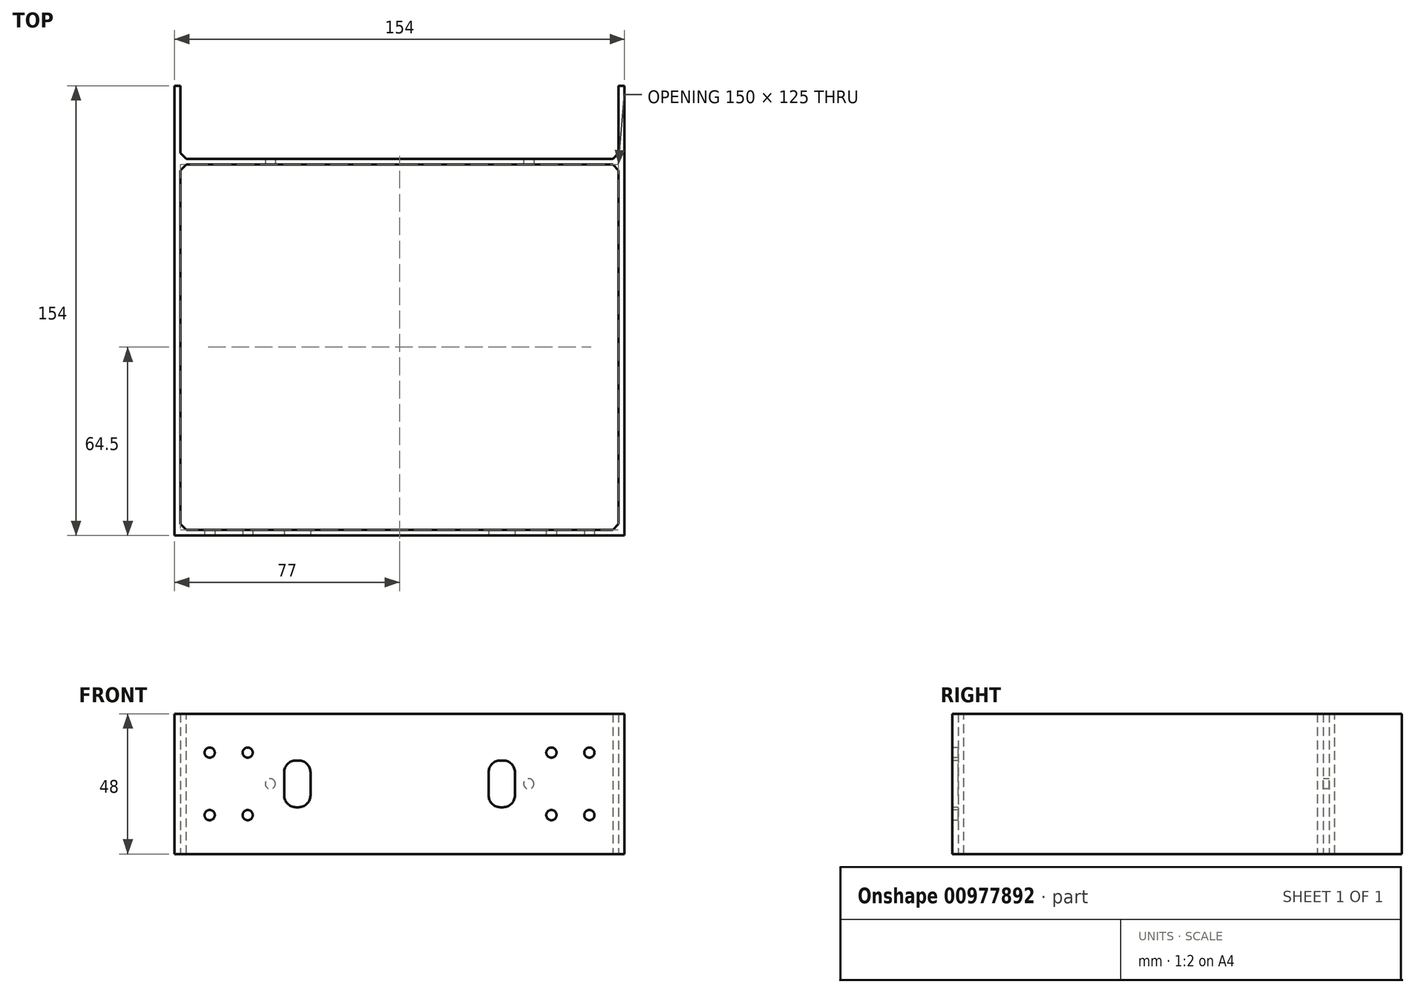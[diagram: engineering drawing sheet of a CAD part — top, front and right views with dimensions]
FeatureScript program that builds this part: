
annotation { "Feature Type Name" : "Feature", "Feature Type Description" : "" }
export const myFeature = defineFeature(function(context is Context, id is Id, definition is map)
    precondition{}
    {
        {
            var Q0;
            Q0=qCreatedBy(makeId("Top.planeOp"),FACE);
            var sketch = newSketch(context, id + "F0", { "sketchPlane" : qUnion([Q0])});
            skLineSegment(sketch, "E0.bottom", {"start": v(75, -62.5) * mm, "end": v(-75, -62.5) * mm});
            skLineSegment(sketch, "E0.top", {"start": v(75, 62.5) * mm, "end": v(-75, 62.5) * mm});
            skLineSegment(sketch, "E0.left", {"start": v(75, -62.5) * mm, "end": v(75, 62.5) * mm});
            skLineSegment(sketch, "E0.right", {"start": v(-75, -62.5) * mm, "end": v(-75, 62.5) * mm});
            skPoint(sketch, "E0.middle", {"position": v(0, 0) * mm});
            skLineSegment(sketch, "E1.0", {"start": v(75, 64.5) * mm, "end": v(-75, 64.5) * mm});
            skLineSegment(sketch, "E1.1", {"start": v(77, -64.5) * mm, "end": v(77, 64.5) * mm});
            skLineSegment(sketch, "E1.2", {"start": v(77, -64.5) * mm, "end": v(-77, -64.5) * mm});
            skLineSegment(sketch, "E1.3", {"start": v(-77, -64.5) * mm, "end": v(-77, 64.5) * mm});
            skLineSegment(sketch, "E2", {"start": v(-77, 64.5) * mm, "end": v(-77, 89.5) * mm});
            skLineSegment(sketch, "E3", {"start": v(-77, 89.5) * mm, "end": v(-75, 89.5) * mm});
            skLineSegment(sketch, "E4", {"start": v(-75, 89.5) * mm, "end": v(-75, 64.5) * mm});
            skLineSegment(sketch, "E5", {"start": v(77, 64.5) * mm, "end": v(77, 89.5) * mm});
            skLineSegment(sketch, "E6", {"start": v(77, 89.5) * mm, "end": v(75, 89.5) * mm});
            skLineSegment(sketch, "E7", {"start": v(75, 89.5) * mm, "end": v(75, 64.5) * mm});
            skSolve(sketch);
        }
        {
            var Q0;
            Q0=makeQuery(id+"F0.imprint","IMPRINT",FACE,{"disambiguationData":[TD([[makeQuery(id+"F0.imprint","IMPRINT",EDGE,{"derivedFrom":sQuery(id+"F0.wireOp",EDGE,"E0.bottom")}),1.0]])]});
            extrude(context, id + "F1", {"entities" : qUnion([Q0]), "depth" : 48 * mm, "offsetDistance" : 25 * mm});
        }
        {
            var Q0;
            Q0=makeQuery(id+"F1.opExtrude","SWEPT_FACE",FACE,{"disambiguationData":[OSD([sQuery(id+"F0.wireOp",EDGE,"E1.2")])]});
            var sketch = newSketch(context, id + "F2", { "sketchPlane" : qUnion([Q0])});
            skPoint(sketch, "E8", {"position": v(-65, 34.7) * mm});
            skPoint(sketch, "E9", {"position": v(-52, 34.7) * mm});
            skPoint(sketch, "E10", {"position": v(-65, 13.3) * mm});
            skPoint(sketch, "E11", {"position": v(-52, 13.3) * mm});
            skCircle(sketch, "E12", {"center": v(-65, 34.7) * mm, "radius": 1.75 * mm});
            skCircle(sketch, "E13", {"center": v(-52, 34.7) * mm, "radius": 1.75 * mm});
            skCircle(sketch, "E14", {"center": v(-65, 13.3) * mm, "radius": 1.75 * mm});
            skCircle(sketch, "E15", {"center": v(-52, 13.3) * mm, "radius": 1.75 * mm});
            skPoint(sketch, "E16", {"position": v(65, 34.7) * mm});
            skPoint(sketch, "E17", {"position": v(52, 34.7) * mm});
            skPoint(sketch, "E18", {"position": v(65, 13.3) * mm});
            skPoint(sketch, "E19", {"position": v(52, 13.3) * mm});
            skCircle(sketch, "E20", {"center": v(52, 34.7) * mm, "radius": 1.75 * mm});
            skCircle(sketch, "E21", {"center": v(65, 34.7) * mm, "radius": 1.75 * mm});
            skCircle(sketch, "E22", {"center": v(52, 13.3) * mm, "radius": 1.75 * mm});
            skCircle(sketch, "E23", {"center": v(65, 13.3) * mm, "radius": 1.75 * mm});
            skPoint(sketch, "E24", {"position": v(-35, 24) * mm});
            skPoint(sketch, "E24.positionSnap0", {"position": v(-77, 24) * mm});
            skPoint(sketch, "E25", {"position": v(35, 24) * mm});
            skPoint(sketch, "E25.positionSnap0", {"position": v(77, 24) * mm});
            skLineSegment(sketch, "E26.bottom", {"start": v(-30.5, 16) * mm, "end": v(-39.5, 16) * mm});
            skLineSegment(sketch, "E26.top", {"start": v(-30.5, 32) * mm, "end": v(-39.5, 32) * mm});
            skLineSegment(sketch, "E26.left", {"start": v(-30.5, 16) * mm, "end": v(-30.5, 32) * mm});
            skLineSegment(sketch, "E26.right", {"start": v(-39.5, 16) * mm, "end": v(-39.5, 32) * mm});
            skLineSegment(sketch, "E27.bottom", {"start": v(30.5, 16) * mm, "end": v(39.5, 16) * mm});
            skLineSegment(sketch, "E27.top", {"start": v(30.5, 32) * mm, "end": v(39.5, 32) * mm});
            skLineSegment(sketch, "E27.left", {"start": v(30.5, 16) * mm, "end": v(30.5, 32) * mm});
            skLineSegment(sketch, "E27.right", {"start": v(39.5, 16) * mm, "end": v(39.5, 32) * mm});
            skSolve(sketch);
        }
        {
            var Q0;
            Q0 = qSketchRegion(id + "F2", true);
            extrude(context, id + "F3", {"entities" : qUnion([Q0]), "operationType" : NewBodyOperationType.REMOVE, "oppositeDirection" : true, "depth" : 2 * mm, "offsetDistance" : 25 * mm});
        }
        {
            var Q0;
            Q0=makeQuery(id+"F1.opExtrude","SWEPT_FACE",FACE,{"disambiguationData":[OSD([sQuery(id+"F0.wireOp",EDGE,"E0.top")])]});
            var sketch = newSketch(context, id + "F4", { "sketchPlane" : qUnion([Q0])});
            skLineSegment(sketch, "E28", {"start": v(-75, 24) * mm, "end": v(75, 24) * mm, "construction": true});
            skPoint(sketch, "E29", {"position": v(-44.25, 24) * mm});
            skPoint(sketch, "E30", {"position": v(44.25, 24) * mm});
            skCircle(sketch, "E31", {"center": v(-44.25, 24) * mm, "radius": 1.75 * mm});
            skCircle(sketch, "E32", {"center": v(44.25, 24) * mm, "radius": 1.75 * mm});
            skLineSegment(sketch, "E33", {"start": v(0, 48) * mm, "end": v(0, 0) * mm, "construction": true});
            skSolve(sketch);
        }
        {
            var Q0;
            Q0 = qSketchRegion(id + "F4", true);
            extrude(context, id + "F5", {"entities" : qUnion([Q0]), "operationType" : NewBodyOperationType.REMOVE, "oppositeDirection" : true, "depth" : 2 * mm, "offsetDistance" : 25 * mm});
        }
        {
            var Q0;
            Q0=makeQuery(id+"F1Yi1FitlM4Pbsa_1.boolean.opBoolean","MERGE",EDGE,{"derivedFrom":[makeQuery(id+"FpN9lTTUDBUBIeG_1.merge.Fbd3ITTwiYVNhud_0.opExtrude","CAP_EDGE",EDGE,{"disambiguationData":[OSD([sQuery(id+"FpN9lTTUDBUBIeG_1.merge.FpALkRZBums56Zn_0.wireOp",EDGE,"iWPo67wE-opZh-09zR-ElC4-vLw7oskhnN67")])],"isStart":false}),makeQuery(id+"F1Yi1FitlM4Pbsa_1.opExtrude","CAP_EDGE",EDGE,{"disambiguationData":[OSD([sQuery(id+"FOdDt70km28mKp0_1.wireOp",EDGE,"o3MTPloT-z9tu-i9GF-FzIv-mRheWzs3rAbh")])],"isStart":true}),makeQuery(id+"F1Yi1FitlM4Pbsa_1.opExtrude","CAP_EDGE",EDGE,{"disambiguationData":[OSD([sQuery(id+"FOdDt70km28mKp0_1.wireOp",EDGE,"GZweiw0S-sn09-VxwW-pDzr-jQGBGms9u5C2")])],"isStart":true})]});
            var Q1;
            Q1=makeQuery(id+"F1Yi1FitlM4Pbsa_1.boolean.opBoolean","MERGE",EDGE,{"derivedFrom":[makeQuery(id+"FpN9lTTUDBUBIeG_1.merge.Fbd3ITTwiYVNhud_0.opExtrude","CAP_EDGE",EDGE,{"disambiguationData":[OSD([sQuery(id+"FpN9lTTUDBUBIeG_1.merge.FpALkRZBums56Zn_0.wireOp",EDGE,"iWPo67wE-opZh-09zR-ElC4-vLw7oskhnN67")])],"isStart":true}),makeQuery(id+"F1Yi1FitlM4Pbsa_1.opExtrude","CAP_EDGE",EDGE,{"disambiguationData":[OSD([sQuery(id+"FOdDt70km28mKp0_1.wireOp",EDGE,"o3MTPloT-z9tu-i9GF-FzIv-mRheWzs3rAbh")])],"isStart":false}),makeQuery(id+"F1Yi1FitlM4Pbsa_1.opExtrude","CAP_EDGE",EDGE,{"disambiguationData":[OSD([sQuery(id+"FOdDt70km28mKp0_1.wireOp",EDGE,"GZweiw0S-sn09-VxwW-pDzr-jQGBGms9u5C2")])],"isStart":false})]});
            var Q2;
            Q2=makeQuery(id+"F1Yi1FitlM4Pbsa_1.opExtrude","SWEPT_EDGE",EDGE,{"disambiguationData":[OSD([sQuery(id+"FOdDt70km28mKp0_1.wireOp",EDGE,"royF5wWM-E6hz-3UVv-FT7d-6jo60GUab2ae"),sQuery(id+"FOdDt70km28mKp0_1.wireOp",EDGE,"GZweiw0S-sn09-VxwW-pDzr-jQGBGms9u5C2")])]});
            var Q3;
            Q3=makeQuery(id+"F1Yi1FitlM4Pbsa_1.opExtrude","SWEPT_EDGE",EDGE,{"disambiguationData":[OSD([sQuery(id+"FOdDt70km28mKp0_1.wireOp",EDGE,"uIt22xs4-Xfgf-FZh4-s74M-pkd60t8jByls"),sQuery(id+"FOdDt70km28mKp0_1.wireOp",EDGE,"o3MTPloT-z9tu-i9GF-FzIv-mRheWzs3rAbh")])]});
            var Q4;
            Q4=makeQuery(id+"F1.opExtrude","SWEPT_EDGE",EDGE,{"disambiguationData":[OSD([sQuery(id+"F0.wireOp",EDGE,"E0.top"),sQuery(id+"F0.wireOp",EDGE,"E0.right")])]});
            var Q5;
            Q5=makeQuery(id+"F1.opExtrude","SWEPT_EDGE",EDGE,{"disambiguationData":[OSD([sQuery(id+"F0.wireOp",EDGE,"E0.bottom"),sQuery(id+"F0.wireOp",EDGE,"E0.right")])]});
            var Q6;
            Q6=makeQuery(id+"F1.opExtrude","SWEPT_EDGE",EDGE,{"disambiguationData":[OSD([sQuery(id+"F0.wireOp",EDGE,"E0.bottom"),sQuery(id+"F0.wireOp",EDGE,"E0.left")])]});
            var Q7;
            Q7=makeQuery(id+"F1.opExtrude","SWEPT_EDGE",EDGE,{"disambiguationData":[OSD([sQuery(id+"F0.wireOp",EDGE,"E0.top"),sQuery(id+"F0.wireOp",EDGE,"E0.left")])]});
            var Q8;
            Q8=makeQuery(id+"F1.opExtrude","SWEPT_EDGE",EDGE,{"disambiguationData":[OSD([sQuery(id+"F0.wireOp",EDGE,"E1.0"),sQuery(id+"F0.wireOp",EDGE,"E7")])]});
            var Q9;
            Q9=makeQuery(id+"F1.opExtrude","SWEPT_EDGE",EDGE,{"disambiguationData":[OSD([sQuery(id+"F0.wireOp",EDGE,"E1.0"),sQuery(id+"F0.wireOp",EDGE,"E4")])]});
            var Q10;
            Q10=makeQuery(id+"F1Yi1FitlM4Pbsa_1.opExtrude","CAP_EDGE",EDGE,{"disambiguationData":[OSD([sQuery(id+"FOdDt70km28mKp0_1.wireOp",EDGE,"7wWSICsi-4I1N-JUo8-QoSu-PKbGlVT1e49P")])],"isStart":true});
            var Q11;
            Q11=makeQuery(id+"F1Yi1FitlM4Pbsa_1.opExtrude","SWEPT_EDGE",EDGE,{"disambiguationData":[OSD([sQuery(id+"FOdDt70km28mKp0_1.wireOp",EDGE,"uv9byznU-pOjR-9hiC-4igj-g0eliUoqPu2g"),sQuery(id+"FOdDt70km28mKp0_1.wireOp",EDGE,"7wWSICsi-4I1N-JUo8-QoSu-PKbGlVT1e49P")])]});
            var Q12;
            Q12=makeQuery(id+"F1Yi1FitlM4Pbsa_1.opExtrude","CAP_EDGE",EDGE,{"disambiguationData":[OSD([sQuery(id+"FOdDt70km28mKp0_1.wireOp",EDGE,"72vwOB9i-hV1r-Klgs-7nSX-HpyqfbhWyw5S")])],"isStart":true});
            var Q13;
            Q13=makeQuery(id+"F1Yi1FitlM4Pbsa_1.opExtrude","SWEPT_EDGE",EDGE,{"disambiguationData":[OSD([sQuery(id+"FOdDt70km28mKp0_1.wireOp",EDGE,"Kes6H1w9-jgmU-FWc4-paKO-pd63mwICXN2u"),sQuery(id+"FOdDt70km28mKp0_1.wireOp",EDGE,"72vwOB9i-hV1r-Klgs-7nSX-HpyqfbhWyw5S")])]});
            var Q14;
            Q14=makeQuery(id+"F1Yi1FitlM4Pbsa_1.opExtrude","SWEPT_EDGE",EDGE,{"disambiguationData":[OSD([sQuery(id+"FOdDt70km28mKp0_1.wireOp",EDGE,"iiod3cV2-Uq62-4OUM-DxVE-C3jseO9USqzs"),sQuery(id+"FOdDt70km28mKp0_1.wireOp",EDGE,"7wWSICsi-4I1N-JUo8-QoSu-PKbGlVT1e49P")])]});
            var Q15;
            Q15=makeQuery(id+"F1Yi1FitlM4Pbsa_1.opExtrude","CAP_EDGE",EDGE,{"disambiguationData":[OSD([sQuery(id+"FOdDt70km28mKp0_1.wireOp",EDGE,"7wWSICsi-4I1N-JUo8-QoSu-PKbGlVT1e49P")])],"isStart":false});
            var Q16;
            Q16=makeQuery(id+"F1Yi1FitlM4Pbsa_1.opExtrude","CAP_EDGE",EDGE,{"disambiguationData":[OSD([sQuery(id+"FOdDt70km28mKp0_1.wireOp",EDGE,"72vwOB9i-hV1r-Klgs-7nSX-HpyqfbhWyw5S")])],"isStart":false});
            var Q17;
            Q17=makeQuery(id+"F1Yi1FitlM4Pbsa_1.opExtrude","SWEPT_EDGE",EDGE,{"disambiguationData":[OSD([sQuery(id+"FOdDt70km28mKp0_1.wireOp",EDGE,"eayyzCDF-hjd2-jC9s-0Njb-n0IpJJDLMkmX"),sQuery(id+"FOdDt70km28mKp0_1.wireOp",EDGE,"72vwOB9i-hV1r-Klgs-7nSX-HpyqfbhWyw5S")])]});
            chamfer(context, id + "F6", {"entities" : qUnion([Q0, Q1, Q2, Q3, Q4, Q5, Q6, Q7, Q8, Q9, Q10, Q11, Q12, Q13, Q14, Q15, Q16, Q17]), "width" : 2 * mm, "tangentPropagation" : true});
        }
        {
            var Q0;
            Q0=makeQuery(id+"F3.boolean.opBoolean","COPY",EDGE,{"derivedFrom":makeQuery(id+"F3.opExtrude","SWEPT_EDGE",EDGE,{"disambiguationData":[OSD([sQuery(id+"F2.wireOp",EDGE,"E26.bottom"),sQuery(id+"F2.wireOp",EDGE,"E26.right")])]})});
            var Q1;
            Q1=makeQuery(id+"F3.boolean.opBoolean","COPY",EDGE,{"derivedFrom":makeQuery(id+"F3.opExtrude","SWEPT_EDGE",EDGE,{"disambiguationData":[OSD([sQuery(id+"F2.wireOp",EDGE,"E26.bottom"),sQuery(id+"F2.wireOp",EDGE,"E26.left")])]})});
            var Q2;
            Q2=makeQuery(id+"F3.boolean.opBoolean","COPY",EDGE,{"derivedFrom":makeQuery(id+"F3.opExtrude","SWEPT_EDGE",EDGE,{"disambiguationData":[OSD([sQuery(id+"F2.wireOp",EDGE,"E26.top"),sQuery(id+"F2.wireOp",EDGE,"E26.left")])]})});
            var Q3;
            Q3=makeQuery(id+"F3.boolean.opBoolean","COPY",EDGE,{"derivedFrom":makeQuery(id+"F3.opExtrude","SWEPT_EDGE",EDGE,{"disambiguationData":[OSD([sQuery(id+"F2.wireOp",EDGE,"E26.top"),sQuery(id+"F2.wireOp",EDGE,"E26.right")])]})});
            var Q4;
            Q4=makeQuery(id+"F3.boolean.opBoolean","COPY",EDGE,{"derivedFrom":makeQuery(id+"F3.opExtrude","SWEPT_EDGE",EDGE,{"disambiguationData":[OSD([sQuery(id+"F2.wireOp",EDGE,"E27.bottom"),sQuery(id+"F2.wireOp",EDGE,"E27.left")])]})});
            var Q5;
            Q5=makeQuery(id+"F3.boolean.opBoolean","COPY",EDGE,{"derivedFrom":makeQuery(id+"F3.opExtrude","SWEPT_EDGE",EDGE,{"disambiguationData":[OSD([sQuery(id+"F2.wireOp",EDGE,"E27.bottom"),sQuery(id+"F2.wireOp",EDGE,"E27.right")])]})});
            var Q6;
            Q6=makeQuery(id+"F3.boolean.opBoolean","COPY",EDGE,{"derivedFrom":makeQuery(id+"F3.opExtrude","SWEPT_EDGE",EDGE,{"disambiguationData":[OSD([sQuery(id+"F2.wireOp",EDGE,"E27.top"),sQuery(id+"F2.wireOp",EDGE,"E27.right")])]})});
            var Q7;
            Q7=makeQuery(id+"F3.boolean.opBoolean","COPY",EDGE,{"derivedFrom":makeQuery(id+"F3.opExtrude","SWEPT_EDGE",EDGE,{"disambiguationData":[OSD([sQuery(id+"F2.wireOp",EDGE,"E27.top"),sQuery(id+"F2.wireOp",EDGE,"E27.left")])]})});
            fillet(context, id + "F7", {"entities" : qUnion([Q0, Q1, Q2, Q3, Q4, Q5, Q6, Q7]), "radius" : 4 * mm, "tangentPropagation" : true, "allowEdgeOverflow" : false});
        }
    });
